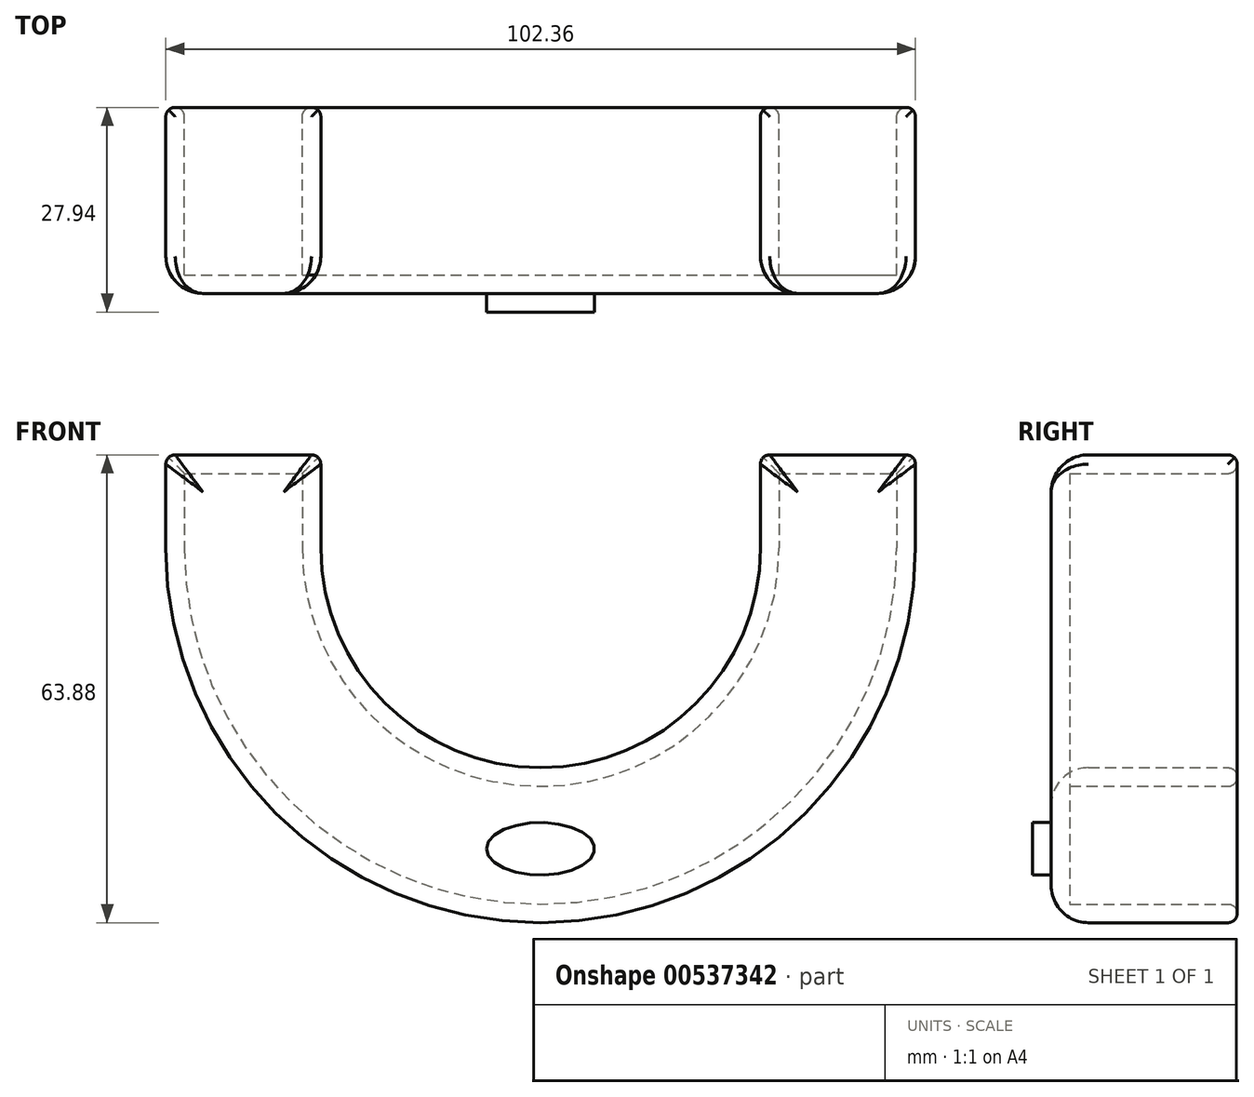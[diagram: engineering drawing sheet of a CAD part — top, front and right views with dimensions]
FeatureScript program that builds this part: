
annotation { "Feature Type Name" : "Feature", "Feature Type Description" : "" }
export const myFeature = defineFeature(function(context is Context, id is Id, definition is map)
    precondition{}
    {
        {
            var Q0;
            Q0=qCreatedBy(makeId("Front.planeOp"),FACE);
            var sketch = newSketch(context, id + "F0", { "sketchPlane" : qUnion([Q0])});
            skCircle(sketch, "E0", {"center": v(0, 0) * mm, "radius": 51.18 * mm});
            skCircle(sketch, "E1", {"center": v(0, 0) * mm, "radius": 30.02 * mm});
            skLineSegment(sketch, "E2", {"start": v(-51.18, 0) * mm, "end": v(-30.02, 0) * mm});
            skLineSegment(sketch, "E3", {"start": v(-30.02, 0) * mm, "end": v(51.18, 0) * mm});
            skSolve(sketch);
        }
        {
            var Q0;
            {var subQ0=sQuery(id+"F0.wireOp",EDGE,"E2");Q0=makeQuery(id+"F0.imprint","IMPRINT",FACE,{"disambiguationData":[TD([[makeQuery(id+"F0.imprint","IMPRINT",EDGE,{"derivedFrom":subQ0}),-1.0]])]});}
            extrude(context, id + "F1", {"entities" : qUnion([Q0]), "depth" : 25.4 * mm, "offsetDistance" : 25.4 * mm});
        }
        {
            var Q0;
            Q0=makeQuery(id+"F1.opExtrude","SWEPT_FACE",FACE,{"disambiguationData":[OSD([sQuery(id+"F0.wireOp",EDGE,"E3")])]});
            var Q1;
            Q1=makeQuery(id+"F1.opExtrude","SWEPT_FACE",FACE,{"disambiguationData":[OSD([sQuery(id+"F0.wireOp",EDGE,"E2")])]});
            extrude(context, id + "F2", {"entities" : qUnion([Q0, Q1]), "operationType" : NewBodyOperationType.ADD, "depth" : 12.7 * mm, "offsetDistance" : 25.4 * mm});
        }
        {
            var Q0;
            {var subQ0=sQuery(id+"F0.wireOp",EDGE,"E3");var subQ1=sQuery(id+"F0.wireOp",EDGE,"E2");Q0=makeQuery(id+"F2.boolean.opBoolean","MERGE",FACE,{"derivedFrom":[makeQuery(id+"F1.opExtrude","CAP_FACE",FACE,{"disambiguationData":[OSD([sQuery(id+"F0.wireOp",EDGE,"E0"),sQuery(id+"F0.wireOp",EDGE,"E1"),subQ1,subQ0])],"isStart":true}),makeQuery(id+"F2.opExtrude","SWEPT_FACE",FACE,{"disambiguationData":[OSD([subQ1]),TDD([makeQuery(id+"F1.opExtrude","CAP_EDGE",EDGE,{"disambiguationData":[OSD([subQ1])],"isStart":true})])]}),makeQuery(id+"F2.opExtrude","SWEPT_FACE",FACE,{"disambiguationData":[OSD([subQ0]),TDD([makeQuery(id+"F1.opExtrude","CAP_EDGE",EDGE,{"disambiguationData":[OSD([subQ0])],"isStart":true})])]})]});}
            shell(context, id + "F3", {"entities" : qUnion([Q0]), "thickness" : 2.54 * mm});
        }
        {
            var Q0;
            {var subQ0=sQuery(id+"F0.wireOp",EDGE,"E0");Q0=makeQuery(id+"F3.opShell","OFFSET_EDGE",EDGE,{"disambiguationData":[OSD([subQ0]),TDD([makeQuery(id+"F1.opExtrude","CAP_EDGE",EDGE,{"disambiguationData":[OSD([subQ0])],"isStart":true})])]});}
            var Q1;
            {var subQ0=sQuery(id+"F0.wireOp",EDGE,"E1");Q1=makeQuery(id+"F3.opShell","OFFSET_EDGE",EDGE,{"disambiguationData":[OSD([subQ0]),TDD([makeQuery(id+"F1.opExtrude","CAP_EDGE",EDGE,{"disambiguationData":[OSD([subQ0])],"isStart":true})])]});}
            var Q2;
            {var subQ0=sQuery(id+"F0.wireOp",EDGE,"E3");var subQ1=sQuery(id+"F0.wireOp",EDGE,"E2");var subQ2=sQuery(id+"F0.wireOp",EDGE,"E1");Q2=makeQuery(id+"F3.opShell","OFFSET_EDGE",EDGE,{"disambiguationData":[OSD([subQ2,subQ1,subQ0]),TDD([makeQuery(id+"F2.opExtrude","SWEPT_EDGE",EDGE,{"disambiguationData":[OSD([subQ2,subQ1,subQ0]),TDD([makeQuery(id+"F1.opExtrude","CAP_VERTEX",VERTEX,{"disambiguationData":[OSD([subQ2,subQ1,subQ0])],"isStart":true})])]})])]});}
            var Q3;
            {var subQ0=sQuery(id+"F0.wireOp",EDGE,"E2");Q3=makeQuery(id+"F3.opShell","OFFSET_EDGE",EDGE,{"disambiguationData":[OSD([subQ0]),TDD([makeQuery(id+"F2.opExtrude","CAP_EDGE",EDGE,{"disambiguationData":[OSD([subQ0]),TDD([makeQuery(id+"F1.opExtrude","CAP_EDGE",EDGE,{"disambiguationData":[OSD([subQ0])],"isStart":true})])],"isStart":false})])]});}
            var Q4;
            {var subQ0=sQuery(id+"F0.wireOp",EDGE,"E2");var subQ1=sQuery(id+"F0.wireOp",EDGE,"E0");Q4=makeQuery(id+"F3.opShell","OFFSET_EDGE",EDGE,{"disambiguationData":[OSD([subQ1,subQ0]),TDD([makeQuery(id+"F2.opExtrude","SWEPT_EDGE",EDGE,{"disambiguationData":[OSD([subQ1,subQ0]),TDD([makeQuery(id+"F1.opExtrude","CAP_VERTEX",VERTEX,{"disambiguationData":[OSD([subQ1,subQ0])],"isStart":true})])]})])]});}
            var Q5;
            {var subQ0=sQuery(id+"F0.wireOp",EDGE,"E3");var subQ1=sQuery(id+"F0.wireOp",EDGE,"E1");Q5=makeQuery(id+"F3.opShell","OFFSET_EDGE",EDGE,{"disambiguationData":[OSD([subQ1,subQ0]),TDD([makeQuery(id+"F2.opExtrude","SWEPT_EDGE",EDGE,{"disambiguationData":[OSD([subQ1,subQ0]),TDD([makeQuery(id+"F1.opExtrude","CAP_VERTEX",VERTEX,{"disambiguationData":[OSD([subQ1,subQ0])],"isStart":true})])]})])]});}
            var Q6;
            {var subQ0=sQuery(id+"F0.wireOp",EDGE,"E3");Q6=makeQuery(id+"F3.opShell","OFFSET_EDGE",EDGE,{"disambiguationData":[OSD([subQ0]),TDD([makeQuery(id+"F2.opExtrude","CAP_EDGE",EDGE,{"disambiguationData":[OSD([subQ0]),TDD([makeQuery(id+"F1.opExtrude","CAP_EDGE",EDGE,{"disambiguationData":[OSD([subQ0])],"isStart":true})])],"isStart":false})])]});}
            var Q7;
            {var subQ0=sQuery(id+"F0.wireOp",EDGE,"E3");var subQ1=sQuery(id+"F0.wireOp",EDGE,"E0");Q7=makeQuery(id+"F3.opShell","OFFSET_EDGE",EDGE,{"disambiguationData":[OSD([subQ1,subQ0]),TDD([makeQuery(id+"F2.opExtrude","SWEPT_EDGE",EDGE,{"disambiguationData":[OSD([subQ1,subQ0]),TDD([makeQuery(id+"F1.opExtrude","CAP_VERTEX",VERTEX,{"disambiguationData":[OSD([subQ1,subQ0])],"isStart":true})])]})])]});}
            var Q8;
            Q8=makeQuery(id+"F1.opExtrude","CAP_EDGE",EDGE,{"disambiguationData":[OSD([sQuery(id+"F0.wireOp",EDGE,"E0")])],"isStart":true});
            var Q9;
            {var subQ0=sQuery(id+"F0.wireOp",EDGE,"E3");var subQ1=sQuery(id+"F0.wireOp",EDGE,"E0");Q9=makeQuery(id+"F2.opExtrude","SWEPT_EDGE",EDGE,{"disambiguationData":[OSD([subQ1,subQ0]),TDD([makeQuery(id+"F1.opExtrude","CAP_VERTEX",VERTEX,{"disambiguationData":[OSD([subQ1,subQ0])],"isStart":true})])]});}
            var Q10;
            {var subQ0=sQuery(id+"F0.wireOp",EDGE,"E3");Q10=makeQuery(id+"F2.opExtrude","CAP_EDGE",EDGE,{"disambiguationData":[OSD([subQ0]),TDD([makeQuery(id+"F1.opExtrude","CAP_EDGE",EDGE,{"disambiguationData":[OSD([subQ0])],"isStart":true})])],"isStart":false});}
            var Q11;
            {var subQ0=sQuery(id+"F0.wireOp",EDGE,"E3");var subQ1=sQuery(id+"F0.wireOp",EDGE,"E1");Q11=makeQuery(id+"F2.opExtrude","SWEPT_EDGE",EDGE,{"disambiguationData":[OSD([subQ1,subQ0]),TDD([makeQuery(id+"F1.opExtrude","CAP_VERTEX",VERTEX,{"disambiguationData":[OSD([subQ1,subQ0])],"isStart":true})])]});}
            var Q12;
            Q12=makeQuery(id+"F1.opExtrude","CAP_EDGE",EDGE,{"disambiguationData":[OSD([sQuery(id+"F0.wireOp",EDGE,"E1")])],"isStart":true});
            var Q13;
            {var subQ0=sQuery(id+"F0.wireOp",EDGE,"E3");var subQ1=sQuery(id+"F0.wireOp",EDGE,"E2");var subQ2=sQuery(id+"F0.wireOp",EDGE,"E1");Q13=makeQuery(id+"F2.opExtrude","SWEPT_EDGE",EDGE,{"disambiguationData":[OSD([subQ2,subQ1,subQ0]),TDD([makeQuery(id+"F1.opExtrude","CAP_VERTEX",VERTEX,{"disambiguationData":[OSD([subQ2,subQ1,subQ0])],"isStart":true})])]});}
            var Q14;
            {var subQ0=sQuery(id+"F0.wireOp",EDGE,"E2");Q14=makeQuery(id+"F2.opExtrude","CAP_EDGE",EDGE,{"disambiguationData":[OSD([subQ0]),TDD([makeQuery(id+"F1.opExtrude","CAP_EDGE",EDGE,{"disambiguationData":[OSD([subQ0])],"isStart":true})])],"isStart":false});}
            var Q15;
            {var subQ0=sQuery(id+"F0.wireOp",EDGE,"E2");var subQ1=sQuery(id+"F0.wireOp",EDGE,"E0");Q15=makeQuery(id+"F2.opExtrude","SWEPT_EDGE",EDGE,{"disambiguationData":[OSD([subQ1,subQ0]),TDD([makeQuery(id+"F1.opExtrude","CAP_VERTEX",VERTEX,{"disambiguationData":[OSD([subQ1,subQ0])],"isStart":true})])]});}
            fillet(context, id + "F4", {"entities" : qUnion([Q0, Q1, Q2, Q3, Q4, Q5, Q6, Q7, Q8, Q9, Q10, Q11, Q12, Q13, Q14, Q15]), "radius" : 1.27 * mm, "tangentPropagation" : true, "allowEdgeOverflow" : false});
        }
        {
            var Q0;
            Q0=makeQuery(id+"F2.opExtrude","CAP_EDGE",EDGE,{"disambiguationData":[OSD([sQuery(id+"F0.wireOp",EDGE,"E0"),sQuery(id+"F0.wireOp",EDGE,"E2")])],"isStart":false});
            var Q1;
            Q1=makeQuery(id+"F2.opExtrude","CAP_EDGE",EDGE,{"disambiguationData":[OSD([sQuery(id+"F0.wireOp",EDGE,"E1"),sQuery(id+"F0.wireOp",EDGE,"E3")])],"isStart":false});
            var Q2;
            Q2=makeQuery(id+"F2.opExtrude","CAP_EDGE",EDGE,{"disambiguationData":[OSD([sQuery(id+"F0.wireOp",EDGE,"E1"),sQuery(id+"F0.wireOp",EDGE,"E2"),sQuery(id+"F0.wireOp",EDGE,"E3")])],"isStart":false});
            var Q3;
            Q3=makeQuery(id+"F2.opExtrude","CAP_EDGE",EDGE,{"disambiguationData":[OSD([sQuery(id+"F0.wireOp",EDGE,"E0"),sQuery(id+"F0.wireOp",EDGE,"E3")])],"isStart":false});
            fillet(context, id + "F5", {"entities" : qUnion([Q0, Q1, Q2, Q3]), "radius" : 1.27 * mm, "tangentPropagation" : true, "allowEdgeOverflow" : false});
        }
        {
            var Q0;
            Q0=makeQuery(id+"F1.opExtrude","CAP_EDGE",EDGE,{"disambiguationData":[OSD([sQuery(id+"F0.wireOp",EDGE,"E1")])],"isStart":false});
            fillet(context, id + "F6", {"entities" : qUnion([Q0]), "radius" : 5.08 * mm, "tangentPropagation" : true, "allowEdgeOverflow" : false});
        }
        {
            var Q0;
            {var subQ0=sQuery(id+"F0.wireOp",EDGE,"E3");var subQ1=sQuery(id+"F0.wireOp",EDGE,"E2");Q0=makeQuery(id+"F2.boolean.opBoolean","MERGE",FACE,{"derivedFrom":[makeQuery(id+"F1.opExtrude","CAP_FACE",FACE,{"disambiguationData":[OSD([sQuery(id+"F0.wireOp",EDGE,"E0"),sQuery(id+"F0.wireOp",EDGE,"E1"),subQ1,subQ0])],"isStart":false}),makeQuery(id+"F2.opExtrude","SWEPT_FACE",FACE,{"disambiguationData":[OSD([subQ1]),TDD([makeQuery(id+"F1.opExtrude","CAP_EDGE",EDGE,{"disambiguationData":[OSD([subQ1])],"isStart":false})])]}),makeQuery(id+"F2.opExtrude","SWEPT_FACE",FACE,{"disambiguationData":[OSD([subQ0]),TDD([makeQuery(id+"F1.opExtrude","CAP_EDGE",EDGE,{"disambiguationData":[OSD([subQ0])],"isStart":false})])]})]});}
            var sketch = newSketch(context, id + "F7", { "sketchPlane" : qUnion([Q0])});
            skEllipse(sketch, "E4", {"center": v(0, -41.08) * mm, "majorRadius": 7.38 * mm, "minorRadius": 3.57 * mm, "majorAxis": v(-1, 0)});
            skSolve(sketch);
        }
        {
            var Q0;
            Q0=makeQuery(id+"F7.imprint","IMPRINT",FACE,{"disambiguationData":[TD([[makeQuery(id+"F7.imprint","IMPRINT",EDGE,{"derivedFrom":sQuery(id+"F7.wireOp",EDGE,"E4")}),1.0]])]});
            extrude(context, id + "F8", {"entities" : qUnion([Q0]), "operationType" : NewBodyOperationType.ADD, "depth" : 2.54 * mm, "offsetDistance" : 25.4 * mm});
        }
    });
